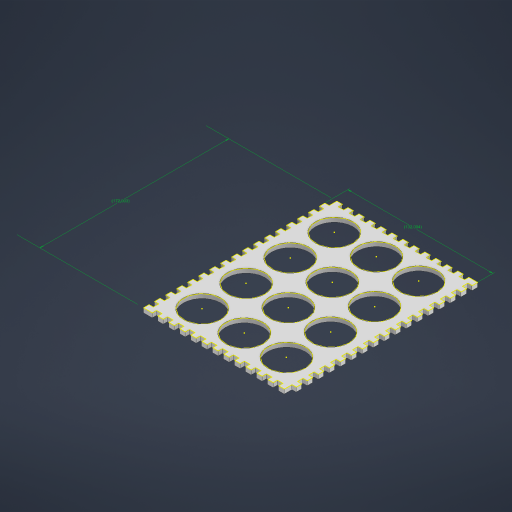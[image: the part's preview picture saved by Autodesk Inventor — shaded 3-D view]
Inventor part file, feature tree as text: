
AUTODESK INVENTOR PART (.ipt)
format: ipt  version: 2023 (Build 270158030, 158C)  size: 947,712 bytes
history: native  units: mm
features: direct_edit x4, sketch x3, extrude x2, delete_face x2, other x2, move_body x2, boolean_combine x1, projected_geometry x1
ambient origin geometry x8: Origin, YZ Plane, XZ Plane, XY Plane, X Axis, Y Axis, Z Axis, Center Point
bodies: Solid1 (feature_tree), Solid2 (feature_tree)
feature tree (17):
  extrude  "Extrusion1"  Depth=5.0mm
  extrude  "Extrusion2"  Depth=130.0mm
  direct_edit  "Direct Edit1"
  boolean_combine  "Combine1"
  direct_edit  "Direct Edit2"
  delete_face  "Delete Face1"
  direct_edit  "Direct Edit3"
  delete_face  "Delete Face2"
  direct_edit  "Direct Edit4"
  sketch  "Sketch4"  dims[d11=4.0mm d12=5.0mm d13=170.0mm d15=10.0mm d16=10.0mm d18=10.0mm d20=5.0mm d21=4.0mm d22=130.0mm d24=10.0mm d25=10.0mm d27=10.0mm d29=4.0mm d30=5.0mm d31=170.0mm d33=10.0mm d34=10.0mm d36=10.0mm d38=4.0mm d39=0.0mm d40=10.02mm d41=10.02mm d42=10.0mm d43=0.0mm d44=0.0mm d45=4.25mm d46=0.0mm d47=0.0mm d48=4.5mm d50=-0.3mm d51=132.004478mm d52=172.003386mm]
  sketch  "Sketch1"  dims[d0=4.0mm d1=0.0mm d2=5.0mm]
  sketch  "Sketch2"  dims[d3=4.0mm d4=130.0mm d6=10.0mm d7=10.0mm d9=10.0mm]
  projected_geometry  "Projected Loop2"
  other  "Scale1"
  move_body  "Move1"
  move_body  "Move2"
  other  "Size1"
